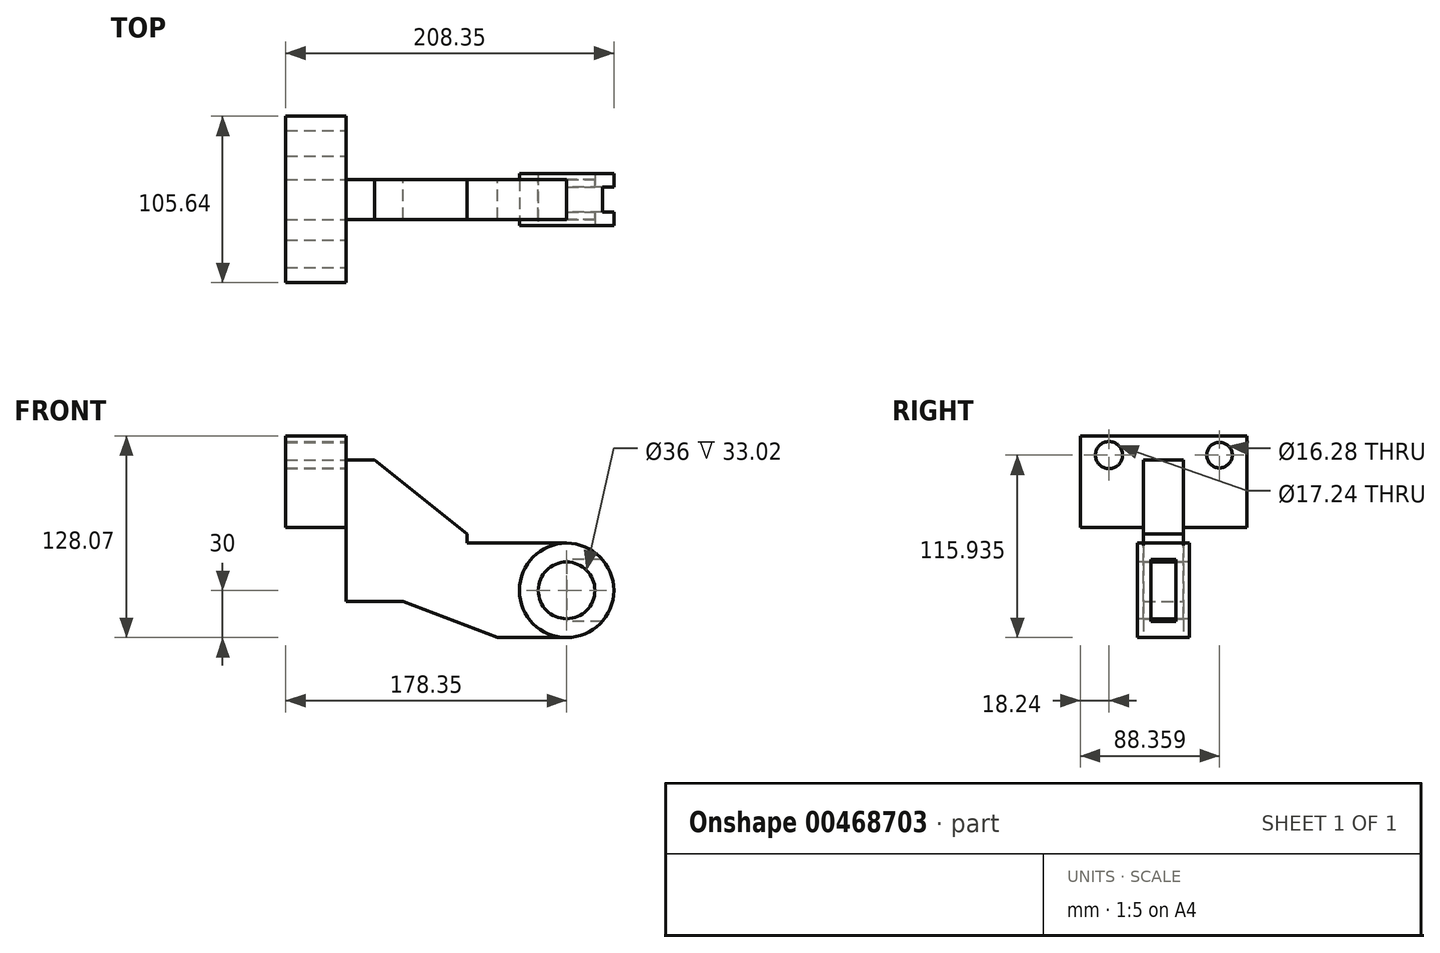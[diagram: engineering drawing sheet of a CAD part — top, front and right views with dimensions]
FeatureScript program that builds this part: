
annotation { "Feature Type Name" : "Feature", "Feature Type Description" : "" }
export const myFeature = defineFeature(function(context is Context, id is Id, definition is map)
    precondition{}
    {
        {
            var Q0;
            Q0=qCreatedBy(makeId("Front.planeOp"),FACE);
            var sketch = newSketch(context, id + "F0", { "sketchPlane" : qUnion([Q0])});
            skCircle(sketch, "E0", {"center": v(0, 0) * mm, "radius": 30 * mm});
            skCircle(sketch, "E1", {"center": v(0, 0) * mm, "radius": 18 * mm});
            skLineSegment(sketch, "E2", {"start": v(0, -30) * mm, "end": v(-44, -30) * mm});
            skLineSegment(sketch, "E3", {"start": v(0, 30) * mm, "end": v(-63.11, 30) * mm});
            skLineSegment(sketch, "E4", {"start": v(-44, -30) * mm, "end": v(-44, 18) * mm});
            skLineSegment(sketch, "E5", {"start": v(-44, 18) * mm, "end": v(-104, 18) * mm});
            skLineSegment(sketch, "E6", {"start": v(-104, 18) * mm, "end": v(-104, -7.15) * mm});
            skLineSegment(sketch, "E7", {"start": v(-140, -7.15) * mm, "end": v(-140, 82.85) * mm});
            skLineSegment(sketch, "E8", {"start": v(-122, -7.15) * mm, "end": v(-122, 82.85) * mm});
            skLineSegment(sketch, "E9", {"start": v(-122, 82.85) * mm, "end": v(-140, 82.85) * mm});
            skLineSegment(sketch, "E10", {"start": v(-63.11, 30) * mm, "end": v(-63.11, 36) * mm});
            skLineSegment(sketch, "E11", {"start": v(-122, 82.85) * mm, "end": v(-63.11, 36) * mm});
            skLineSegment(sketch, "E12", {"start": v(-140, -7.15) * mm, "end": v(-122, -7.15) * mm});
            skLineSegment(sketch, "E13", {"start": v(-122, -7.15) * mm, "end": v(-104, -7.15) * mm});
            skLineSegment(sketch, "E14", {"start": v(-104, -7.15) * mm, "end": v(-44, -30) * mm});
            skLineSegment(sketch, "E15", {"start": v(0, 58.1) * mm, "end": v(0, -49.7) * mm});
            skLineSegment(sketch, "E16", {"start": v(-55.05, 0) * mm, "end": v(62.9, 0) * mm});
            skSolve(sketch);
        }
        {
            var Q0;
            Q0=makeQuery(id+"F0.imprint","IMPRINT",FACE,{"disambiguationData":[TD([[makeQuery(id+"F0.imprint","IMPRINT",EDGE,{"derivedFrom":sQuery(id+"F0.wireOp",EDGE,"E7")}),-1.0]])]});
            var Q1;
            {var subQ0=sQuery(id+"F0.wireOp",EDGE,"E5");Q1=makeQuery(id+"F0.imprint","IMPRINT",FACE,{"disambiguationData":[TD([[makeQuery(id+"F0.imprint","IMPRINT",EDGE,{"derivedFrom":subQ0}),1.0]])]});}
            var Q2;
            {var subQ0=sQuery(id+"F0.wireOp",EDGE,"E15");var subQ1=sQuery(id+"F0.wireOp",EDGE,"E1");var subQ2=makeQuery(id+"F0.imprint","INTERSECT",VERTEX,{"disambiguationData":[OD(0.0)],"derivedFrom":[subQ1,subQ0]});Q2=makeQuery(id+"F0.imprint","IMPRINT",FACE,{"disambiguationData":[TD([[makeQuery(id+"F0.imprint","IMPRINT",EDGE,{"disambiguationData":[TD([[subQ2,1.0]])],"derivedFrom":subQ1}),1.0]])]});}
            var Q3;
            {var subQ0=sQuery(id+"F0.wireOp",EDGE,"E15");var subQ1=sQuery(id+"F0.wireOp",EDGE,"E1");var subQ2=makeQuery(id+"F0.imprint","INTERSECT",VERTEX,{"disambiguationData":[OD(0.0)],"derivedFrom":[subQ1,subQ0]});Q3=makeQuery(id+"F0.imprint","IMPRINT",FACE,{"disambiguationData":[TD([[makeQuery(id+"F0.imprint","IMPRINT",EDGE,{"disambiguationData":[TD([[subQ2,-1.0]])],"derivedFrom":subQ1}),1.0]])]});}
            var Q4;
            {var subQ0=sQuery(id+"F0.wireOp",EDGE,"E16");var subQ1=sQuery(id+"F0.wireOp",EDGE,"E1");var subQ2=makeQuery(id+"F0.imprint","INTERSECT",VERTEX,{"disambiguationData":[OD(1.0)],"derivedFrom":[subQ1,subQ0]});Q4=makeQuery(id+"F0.imprint","IMPRINT",FACE,{"disambiguationData":[TD([[makeQuery(id+"F0.imprint","IMPRINT",EDGE,{"disambiguationData":[TD([[subQ2,-1.0]])],"derivedFrom":subQ1}),1.0]])]});}
            var Q5;
            {var subQ0=sQuery(id+"F0.wireOp",EDGE,"E16");var subQ1=sQuery(id+"F0.wireOp",EDGE,"E1");var subQ2=makeQuery(id+"F0.imprint","INTERSECT",VERTEX,{"disambiguationData":[OD(0.0)],"derivedFrom":[subQ1,subQ0]});Q5=makeQuery(id+"F0.imprint","IMPRINT",FACE,{"disambiguationData":[TD([[makeQuery(id+"F0.imprint","IMPRINT",EDGE,{"disambiguationData":[TD([[subQ2,1.0]])],"derivedFrom":subQ1}),1.0]])]});}
            var Q6;
            {var subQ0=sQuery(id+"F0.wireOp",EDGE,"E2");Q6=makeQuery(id+"F0.imprint","IMPRINT",FACE,{"disambiguationData":[TD([[makeQuery(id+"F0.imprint","IMPRINT",EDGE,{"derivedFrom":subQ0}),-1.0]])]});}
            var Q7;
            {var subQ1=sQuery(id+"F0.wireOp",EDGE,"E3");Q7=makeQuery(id+"F0.imprint","IMPRINT",FACE,{"disambiguationData":[TD([[makeQuery(id+"F0.imprint","IMPRINT",EDGE,{"derivedFrom":subQ1}),1.0]])]});}
            extrude(context, id + "F1", {"entities" : qUnion([Q0, Q1, Q2, Q3, Q4, Q5, Q6, Q7]), "endBound" : BoundingType.SYMMETRIC, "depth" : 25.4 * mm});
        }
        {
            var Q0;
            {var subQ0=sQuery(id+"F0.wireOp",EDGE,"E15");var subQ5=sQuery(id+"F0.wireOp",EDGE,"E1");var subQ6=makeQuery(id+"F0.imprint","INTERSECT",VERTEX,{"disambiguationData":[OD(0.0)],"derivedFrom":[subQ5,subQ0]});Q0=makeQuery(id+"F0.imprint","IMPRINT",FACE,{"disambiguationData":[TD([[makeQuery(id+"F0.imprint","IMPRINT",EDGE,{"disambiguationData":[TD([[subQ6,-1.0]])],"derivedFrom":subQ5}),-1.0]])]});}
            var Q1;
            {var subQ0=sQuery(id+"F0.wireOp",EDGE,"E15");var subQ5=sQuery(id+"F0.wireOp",EDGE,"E1");var subQ7=makeQuery(id+"F0.imprint","INTERSECT",VERTEX,{"disambiguationData":[OD(0.0)],"derivedFrom":[subQ5,subQ0]});Q1=makeQuery(id+"F0.imprint","IMPRINT",FACE,{"disambiguationData":[TD([[makeQuery(id+"F0.imprint","IMPRINT",EDGE,{"disambiguationData":[TD([[subQ7,1.0]])],"derivedFrom":subQ5}),-1.0]])]});}
            var Q2;
            {var subQ3=sQuery(id+"F0.wireOp",EDGE,"E16");var subQ5=sQuery(id+"F0.wireOp",EDGE,"E1");var subQ6=makeQuery(id+"F0.imprint","INTERSECT",VERTEX,{"disambiguationData":[OD(0.0)],"derivedFrom":[subQ5,subQ3]});Q2=makeQuery(id+"F0.imprint","IMPRINT",FACE,{"disambiguationData":[TD([[makeQuery(id+"F0.imprint","IMPRINT",EDGE,{"disambiguationData":[TD([[subQ6,1.0]])],"derivedFrom":subQ5}),-1.0]])]});}
            var Q3;
            {var subQ3=sQuery(id+"F0.wireOp",EDGE,"E16");var subQ5=sQuery(id+"F0.wireOp",EDGE,"E1");var subQ6=makeQuery(id+"F0.imprint","INTERSECT",VERTEX,{"disambiguationData":[OD(1.0)],"derivedFrom":[subQ5,subQ3]});Q3=makeQuery(id+"F0.imprint","IMPRINT",FACE,{"disambiguationData":[TD([[makeQuery(id+"F0.imprint","IMPRINT",EDGE,{"disambiguationData":[TD([[subQ6,-1.0]])],"derivedFrom":subQ5}),-1.0]])]});}
            extrude(context, id + "F2", {"entities" : qUnion([Q0, Q1, Q2, Q3]), "endBound" : BoundingType.SYMMETRIC, "oppositeDirection" : true, "depth" : 33.02 * mm});
        }
        {
            var Q0;
            Q0=makeQuery(id+"F1.opExtrude","SWEPT_FACE",FACE,{"disambiguationData":[OSD([sQuery(id+"F0.wireOp",EDGE,"E7")])]});
            var sketch = newSketch(context, id + "F3", { "sketchPlane" : qUnion([Q0])});
            skLineSegment(sketch, "E17.bottom", {"start": v(-52.82, 98.07) * mm, "end": v(52.82, 98.07) * mm});
            skLineSegment(sketch, "E17.left", {"start": v(-52.82, 98.07) * mm, "end": v(-52.82, 39.82) * mm});
            skLineSegment(sketch, "E17.right", {"start": v(52.82, 98.07) * mm, "end": v(52.82, 39.82) * mm});
            skCircle(sketch, "E18", {"center": v(-35.54, 85.94) * mm, "radius": 8.14 * mm});
            skCircle(sketch, "E19", {"center": v(34.58, 85.94) * mm, "radius": 8.62 * mm});
            skLineSegment(sketch, "E20", {"start": v(-35.54, 85.94) * mm, "end": v(34.58, 85.94) * mm, "construction": true});
            skLineSegment(sketch, "E21", {"start": v(52.82, 39.82) * mm, "end": v(-52.82, 39.82) * mm});
            skSolve(sketch);
        }
        {
            var Q0;
            Q0=makeQuery(id+"F3.imprint","IMPRINT",FACE,{"disambiguationData":[TD([[makeQuery(id+"F3.imprint","IMPRINT",EDGE,{"derivedFrom":sQuery(id+"F3.wireOp",EDGE,"E17.bottom")}),-1.0]])]});
            var Q1;
            Q1=sQuery(id+"F3.wireOp",EDGE,"E17.top");
            var Q2;
            Q2=sQuery(id+"F3.wireOp",EDGE,"E17.left");
            var Q3;
            Q3=sQuery(id+"F3.wireOp",EDGE,"E17.bottom");
            var Q4;
            Q4=sQuery(id+"F3.wireOp",EDGE,"E17.right");
            var Q5;
            Q5=sQuery(id+"F3.wireOp",EDGE,"E18");
            var Q6;
            Q6=sQuery(id+"F3.wireOp",EDGE,"E19");
            extrude(context, id + "F4", {"entities" : qUnion([Q0]), "surfaceEntities" : qUnion([Q1, Q2, Q3, Q4, Q5, Q6]), "depth" : 38.35 * mm});
        }
        {
            var Q0;
            Q0=qCreatedBy(makeId("Right.planeOp"),FACE);
            var sketch = newSketch(context, id + "F5", { "sketchPlane" : qUnion([Q0])});
            skLineSegment(sketch, "E22.bottom", {"start": v(-8.04, 19.62) * mm, "end": v(7.79, 19.62) * mm});
            skLineSegment(sketch, "E22.top", {"start": v(-8.04, -19.62) * mm, "end": v(7.79, -19.62) * mm});
            skLineSegment(sketch, "E22.left", {"start": v(-8.04, 19.62) * mm, "end": v(-8.04, -19.62) * mm});
            skLineSegment(sketch, "E22.right", {"start": v(7.79, 19.62) * mm, "end": v(7.79, -19.62) * mm});
            skSolve(sketch);
        }
        {
            var Q0;
            Q0 = qSketchRegion(id + "F5", true);
            extrude(context, id + "F6", {"entities" : qUnion([Q0]), "operationType" : NewBodyOperationType.REMOVE, "depth" : 56.9 * mm});
        }
    });
